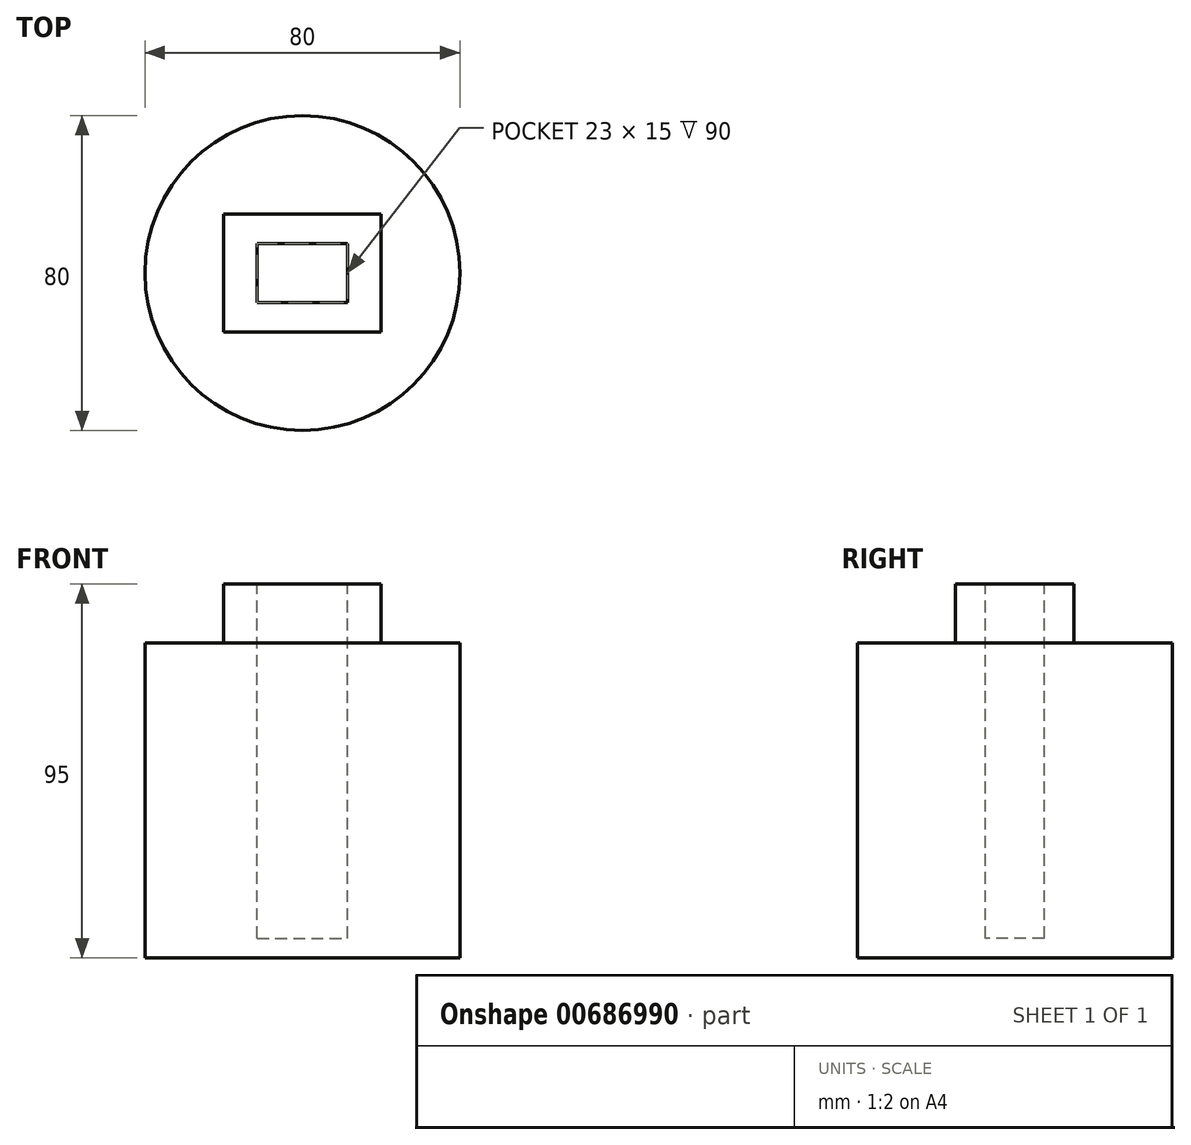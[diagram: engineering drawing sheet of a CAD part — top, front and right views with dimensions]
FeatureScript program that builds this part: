
annotation { "Feature Type Name" : "Feature", "Feature Type Description" : "" }
export const myFeature = defineFeature(function(context is Context, id is Id, definition is map)
    precondition{}
    {
        {
            var Q0;
            Q0=qCreatedBy(makeId("Top.planeOp"),FACE);
            var sketch = newSketch(context, id + "F0", { "sketchPlane" : qUnion([Q0])});
            skCircle(sketch, "E0", {"center": v(0, 0) * mm, "radius": 40 * mm});
            skSolve(sketch);
        }
        {
            var Q0;
            Q0 = qSketchRegion(id + "F0", true);
            extrude(context, id + "F1", {"entities" : qUnion([Q0]), "depth" : 80 * mm, "offsetDistance" : 25 * mm});
        }
        {
            var Q0;
            Q0=makeQuery(id+"F1.opExtrude","CAP_FACE",FACE,{"disambiguationData":[OSD([sQuery(id+"F0.wireOp",EDGE,"E0")])],"isStart":false});
            var sketch = newSketch(context, id + "F2", { "sketchPlane" : qUnion([Q0])});
            skLineSegment(sketch, "E1.bottom", {"start": v(-20, -15) * mm, "end": v(20, -15) * mm});
            skLineSegment(sketch, "E1.top", {"start": v(-20, 15) * mm, "end": v(20, 15) * mm});
            skLineSegment(sketch, "E1.left", {"start": v(-20, -15) * mm, "end": v(-20, 15) * mm});
            skLineSegment(sketch, "E1.right", {"start": v(20, -15) * mm, "end": v(20, 15) * mm});
            skPoint(sketch, "E1.middle", {"position": v(0, 0) * mm});
            skSolve(sketch);
        }
        {
            var Q0;
            Q0 = qSketchRegion(id + "F2", true);
            extrude(context, id + "F3", {"entities" : qUnion([Q0]), "operationType" : NewBodyOperationType.ADD, "depth" : 15 * mm, "offsetDistance" : 25 * mm});
        }
        {
            var Q0;
            Q0=makeQuery(id+"F3.opExtrude","CAP_FACE",FACE,{"disambiguationData":[OSD([sQuery(id+"F2.wireOp",EDGE,"E1.bottom"),sQuery(id+"F2.wireOp",EDGE,"E1.top"),sQuery(id+"F2.wireOp",EDGE,"E1.left"),sQuery(id+"F2.wireOp",EDGE,"E1.right")])],"isStart":false});
            var sketch = newSketch(context, id + "F4", { "sketchPlane" : qUnion([Q0])});
            skLineSegment(sketch, "E2.bottom", {"start": v(-11.5, 7.5) * mm, "end": v(11.5, 7.5) * mm});
            skLineSegment(sketch, "E2.top", {"start": v(-11.5, -7.5) * mm, "end": v(11.5, -7.5) * mm});
            skLineSegment(sketch, "E2.left", {"start": v(-11.5, 7.5) * mm, "end": v(-11.5, -7.5) * mm});
            skLineSegment(sketch, "E2.right", {"start": v(11.5, 7.5) * mm, "end": v(11.5, -7.5) * mm});
            skPoint(sketch, "E2.middle", {"position": v(0, 0) * mm});
            skSolve(sketch);
        }
        {
            var Q0;
            Q0 = qSketchRegion(id + "F4", true);
            extrude(context, id + "F5", {"entities" : qUnion([Q0]), "operationType" : NewBodyOperationType.REMOVE, "oppositeDirection" : true, "depth" : 90 * mm, "offsetDistance" : 25 * mm});
        }
    });
